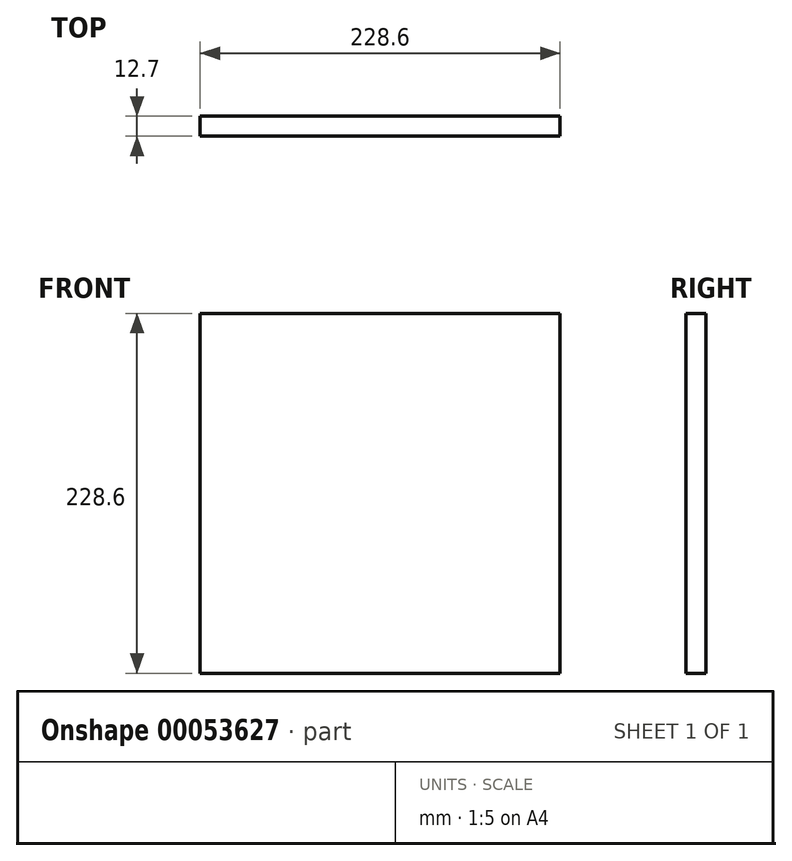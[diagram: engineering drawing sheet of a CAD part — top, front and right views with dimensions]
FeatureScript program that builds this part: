
annotation { "Feature Type Name" : "Feature", "Feature Type Description" : "" }
export const myFeature = defineFeature(function(context is Context, id is Id, definition is map)
    precondition{}
    {
        {
            var Q0;
            Q0=qCreatedBy(makeId("Front.planeOp"),FACE);
            var sketch = newSketch(context, id + "F0", { "sketchPlane" : qUnion([Q0])});
            skLineSegment(sketch, "E0.bottom", {"start": v(-114.3, 114.3) * mm, "end": v(114.3, 114.3) * mm});
            skLineSegment(sketch, "E0.top", {"start": v(-114.3, -114.3) * mm, "end": v(114.3, -114.3) * mm});
            skLineSegment(sketch, "E0.left", {"start": v(-114.3, 114.3) * mm, "end": v(-114.3, -114.3) * mm});
            skLineSegment(sketch, "E0.right", {"start": v(114.3, 114.3) * mm, "end": v(114.3, -114.3) * mm});
            skSolve(sketch);
        }
        {
            var Q0;
            Q0=makeQuery(id+"F0.imprint","IMPRINT",FACE,{"disambiguationData":[TD([[makeQuery(id+"F0.imprint","IMPRINT",EDGE,{"derivedFrom":sQuery(id+"F0.wireOp",EDGE,"E0.bottom")}),-1.0]])]});
            extrude(context, id + "F1", {"entities" : qUnion([Q0]), "depth" : 12.7 * mm});
        }
    });
